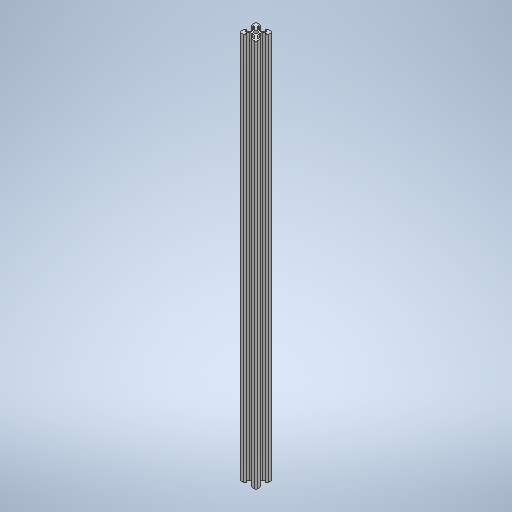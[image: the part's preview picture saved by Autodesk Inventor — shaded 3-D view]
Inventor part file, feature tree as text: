
AUTODESK INVENTOR PART (.ipt)
format: ipt  version: 2025.2 (Build 292293000, 293)  size: 404,992 bytes
history: native  units: mm
features: other x1, extrude x1, sketch x1
ambient origin geometry x8: Origin, YZ Plane, XZ Plane, XY Plane, X Axis, Y Axis, Z Axis, Center Point
bodies: Body1 (feature_tree)
feature tree (3):
  other  "Твердое тело1"
  extrude  "Выдавливание1"  Depth=0.25mm
  sketch  "Эскиз1"
